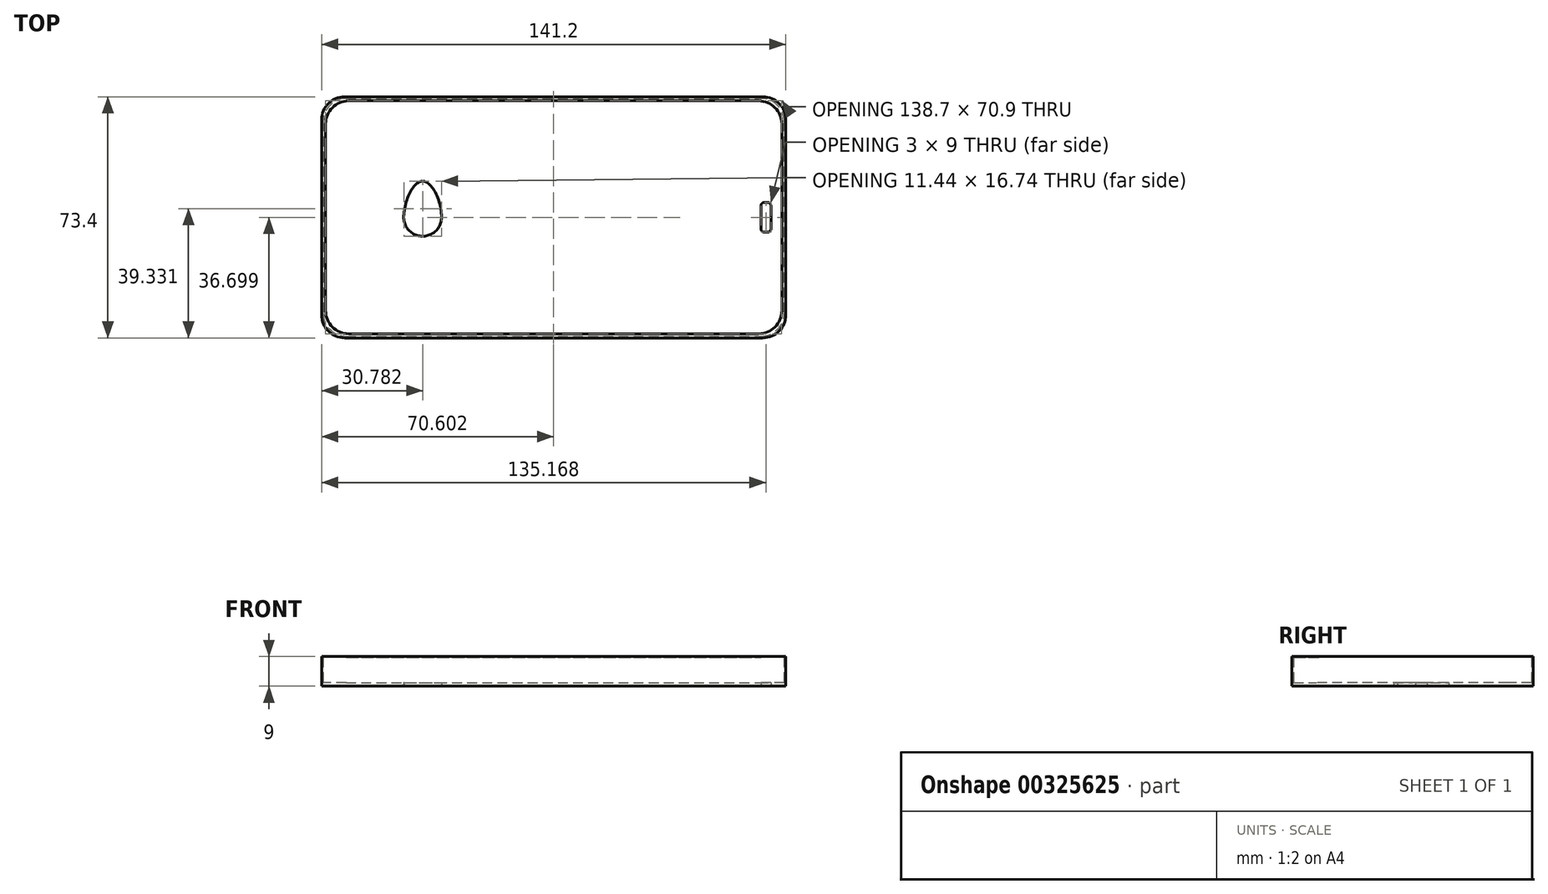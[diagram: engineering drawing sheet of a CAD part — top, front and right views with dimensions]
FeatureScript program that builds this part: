
annotation { "Feature Type Name" : "Feature", "Feature Type Description" : "" }
export const myFeature = defineFeature(function(context is Context, id is Id, definition is map)
    precondition{}
    {
        {
            var Q0;
            Q0=qCreatedBy(makeId("Top.planeOp"),FACE);
            var sketch = newSketch(context, id + "F0", { "sketchPlane" : qUnion([Q0])});
            skLineSegment(sketch, "E0.bottom", {"start": v(-97.78, 46.92) * mm, "end": v(28.42, 46.92) * mm});
            skLineSegment(sketch, "E0.top", {"start": v(-97.78, -25.48) * mm, "end": v(28.42, -25.48) * mm});
            skLineSegment(sketch, "E0.left", {"start": v(-104.78, 39.92) * mm, "end": v(-104.78, -18.48) * mm});
            skLineSegment(sketch, "E0.right", {"start": v(35.42, 39.92) * mm, "end": v(35.42, -18.48) * mm});
            skLineSegment(sketch, "E1.bottom", {"start": v(-98.28, 47.42) * mm, "end": v(28.92, 47.42) * mm});
            skLineSegment(sketch, "E1.top", {"start": v(-98.28, -25.98) * mm, "end": v(28.92, -25.98) * mm});
            skLineSegment(sketch, "E1.left", {"start": v(-105.28, 40.42) * mm, "end": v(-105.28, -18.98) * mm});
            skLineSegment(sketch, "E1.right", {"start": v(35.92, 40.42) * mm, "end": v(35.92, -18.98) * mm});
            skLineSegment(sketch, "E2.bottom", {"start": v(-97.03, 46.17) * mm, "end": v(27.67, 46.17) * mm});
            skLineSegment(sketch, "E2.top", {"start": v(-97.03, -24.73) * mm, "end": v(27.67, -24.73) * mm});
            skLineSegment(sketch, "E2.left", {"start": v(-104.03, 39.17) * mm, "end": v(-104.03, -17.73) * mm});
            skLineSegment(sketch, "E2.right", {"start": v(34.67, 39.17) * mm, "end": v(34.67, -17.73) * mm});
            skPoint(sketch, "E3", {"position": v(-104.78, 10.72) * mm});
            skLineSegment(sketch, "E4", {"start": v(-104.78, 10.72) * mm, "end": v(-79.78, 10.72) * mm});
            skPoint(sketch, "E4.endSnap0", {"position": v(-104.03, 10.72) * mm});
            skLineSegment(sketch, "E5", {"start": v(-79.78, 10.72) * mm, "end": v(-68.78, 10.72) * mm});
            skPoint(sketch, "E6", {"position": v(-80.25, 10.72) * mm});
            skPoint(sketch, "E7", {"position": v(-74.53, 10.72) * mm});
            skCircle(sketch, "E8", {"center": v(-74.53, 10.72) * mm, "radius": 5.75 * mm});
            skLineSegment(sketch, "E9", {"start": v(-74.53, 10.72) * mm, "end": v(-74.53, 21.72) * mm});
            skFitSpline(sketch, "E10", {"points": [v(-80.25, 10.72) * mm, v(-74.53, 21.72) * mm, v(-68.78, 10.72) * mm], "startDerivative": vector(0, 29.93) * mm, "endDerivative": vector(0, -29.91) * mm});
            skLineSegment(sketch, "E11.bottom", {"start": v(29.3, 15.22) * mm, "end": v(30.48, 15.22) * mm});
            skLineSegment(sketch, "E11.top", {"start": v(29.3, 6.22) * mm, "end": v(30.48, 6.22) * mm});
            skLineSegment(sketch, "E11.left", {"start": v(28.39, 14.31) * mm, "end": v(28.39, 7.12) * mm});
            skLineSegment(sketch, "E11.right", {"start": v(31.39, 14.31) * mm, "end": v(31.39, 7.12) * mm});
            skPoint(sketch, "E12.visualSharp", {"position": v(28.39, 15.22) * mm});
            skArc(sketch, "E12.filletArc", {"start": v(29.3, 15.22) * mm, "mid": v(28.65, 14.95) * mm, "end": v(28.39, 14.31) * mm});
            skPoint(sketch, "E13.visualSharp", {"position": v(31.39, 15.22) * mm});
            skArc(sketch, "E13.filletArc", {"start": v(31.39, 14.31) * mm, "mid": v(31.12, 14.95) * mm, "end": v(30.48, 15.22) * mm});
            skPoint(sketch, "E14.visualSharp", {"position": v(31.39, 6.22) * mm});
            skArc(sketch, "E14.filletArc", {"start": v(30.48, 6.22) * mm, "mid": v(31.12, 6.48) * mm, "end": v(31.39, 7.12) * mm});
            skPoint(sketch, "E15.visualSharp", {"position": v(28.39, 6.22) * mm});
            skArc(sketch, "E15.filletArc", {"start": v(28.39, 7.12) * mm, "mid": v(28.65, 6.48) * mm, "end": v(29.3, 6.22) * mm});
            skPoint(sketch, "E16.visualSharp", {"position": v(-105.28, 47.42) * mm});
            skArc(sketch, "E16.filletArc", {"start": v(-98.28, 47.42) * mm, "mid": v(-103.23, 45.37) * mm, "end": v(-105.28, 40.42) * mm});
            skPoint(sketch, "E17.visualSharp", {"position": v(-104.78, 46.92) * mm});
            skArc(sketch, "E17.filletArc", {"start": v(-97.78, 46.92) * mm, "mid": v(-102.73, 44.87) * mm, "end": v(-104.78, 39.92) * mm});
            skPoint(sketch, "E18.visualSharp", {"position": v(-104.03, 46.17) * mm});
            skArc(sketch, "E18.filletArc", {"start": v(-97.03, 46.17) * mm, "mid": v(-101.98, 44.12) * mm, "end": v(-104.03, 39.17) * mm});
            skPoint(sketch, "E19.visualSharp", {"position": v(-105.28, -25.98) * mm});
            skArc(sketch, "E19.filletArc", {"start": v(-105.28, -18.98) * mm, "mid": v(-103.23, -23.93) * mm, "end": v(-98.28, -25.98) * mm});
            skPoint(sketch, "E20.visualSharp", {"position": v(-104.78, -25.48) * mm});
            skArc(sketch, "E20.filletArc", {"start": v(-104.78, -18.48) * mm, "mid": v(-102.73, -23.43) * mm, "end": v(-97.78, -25.48) * mm});
            skPoint(sketch, "E21.visualSharp", {"position": v(-104.03, -24.73) * mm});
            skArc(sketch, "E21.filletArc", {"start": v(-104.03, -17.73) * mm, "mid": v(-101.98, -22.68) * mm, "end": v(-97.03, -24.73) * mm});
            skPoint(sketch, "E22.visualSharp", {"position": v(34.67, -24.73) * mm});
            skArc(sketch, "E22.filletArc", {"start": v(27.67, -24.73) * mm, "mid": v(32.62, -22.68) * mm, "end": v(34.67, -17.73) * mm});
            skPoint(sketch, "E23.visualSharp", {"position": v(35.42, -25.48) * mm});
            skArc(sketch, "E23.filletArc", {"start": v(28.42, -25.48) * mm, "mid": v(33.37, -23.43) * mm, "end": v(35.42, -18.48) * mm});
            skPoint(sketch, "E24.visualSharp", {"position": v(35.92, -25.98) * mm});
            skArc(sketch, "E24.filletArc", {"start": v(28.92, -25.98) * mm, "mid": v(33.87, -23.93) * mm, "end": v(35.92, -18.98) * mm});
            skPoint(sketch, "E25.visualSharp", {"position": v(34.67, 46.17) * mm});
            skArc(sketch, "E25.filletArc", {"start": v(34.67, 39.17) * mm, "mid": v(32.62, 44.12) * mm, "end": v(27.67, 46.17) * mm});
            skPoint(sketch, "E26.visualSharp", {"position": v(35.42, 46.92) * mm});
            skArc(sketch, "E26.filletArc", {"start": v(35.42, 39.92) * mm, "mid": v(33.37, 44.87) * mm, "end": v(28.42, 46.92) * mm});
            skPoint(sketch, "E27.visualSharp", {"position": v(35.92, 47.42) * mm});
            skArc(sketch, "E27.filletArc", {"start": v(35.92, 40.42) * mm, "mid": v(33.87, 45.37) * mm, "end": v(28.92, 47.42) * mm});
            skSolve(sketch);
        }
        {
            var Q0;
            Q0=makeQuery(id+"F0.imprint","IMPRINT",FACE,{"disambiguationData":[TD([[makeQuery(id+"F0.imprint","IMPRINT",EDGE,{"derivedFrom":sQuery(id+"F0.wireOp",EDGE,"E0.bottom")}),1.0]])]});
            extrude(context, id + "F1", {"entities" : qUnion([Q0]), "depth" : 9 * mm});
        }
        {
            var Q0;
            Q0=makeQuery(id+"F0.imprint","IMPRINT",FACE,{"disambiguationData":[TD([[makeQuery(id+"F0.imprint","IMPRINT",EDGE,{"derivedFrom":sQuery(id+"F0.wireOp",EDGE,"E2.bottom")}),-1.0]])]});
            var Q1;
            Q1=makeQuery(id+"F0.imprint","IMPRINT",FACE,{"disambiguationData":[TD([[makeQuery(id+"F0.imprint","IMPRINT",EDGE,{"derivedFrom":sQuery(id+"F0.wireOp",EDGE,"E0.bottom")}),-1.0]])]});
            var Q2;
            Q2=makeQuery(id+"F0.imprint","IMPRINT",FACE,{"disambiguationData":[TD([[makeQuery(id+"F0.imprint","IMPRINT",EDGE,{"derivedFrom":sQuery(id+"F0.wireOp",EDGE,"E0.bottom")}),1.0]])]});
            extrude(context, id + "F2", {"entities" : qUnion([Q0, Q1, Q2]), "operationType" : NewBodyOperationType.ADD, "depth" : 1 * mm});
        }
        {
            var Q0;
            Q0=makeQuery(id+"F0.imprint","IMPRINT",FACE,{"disambiguationData":[TD([[makeQuery(id+"F0.imprint","IMPRINT",EDGE,{"derivedFrom":sQuery(id+"F0.wireOp",EDGE,"E0.bottom")}),-1.0]])]});
            extrude(context, id + "F3", {"entities" : qUnion([Q0]), "operationType" : NewBodyOperationType.ADD, "depth" : 9 * mm, "hasSecondDirection" : true, "secondDirectionOppositeDirection" : false, "secondDirectionDepth" : 8.8 * mm});
        }
    });
